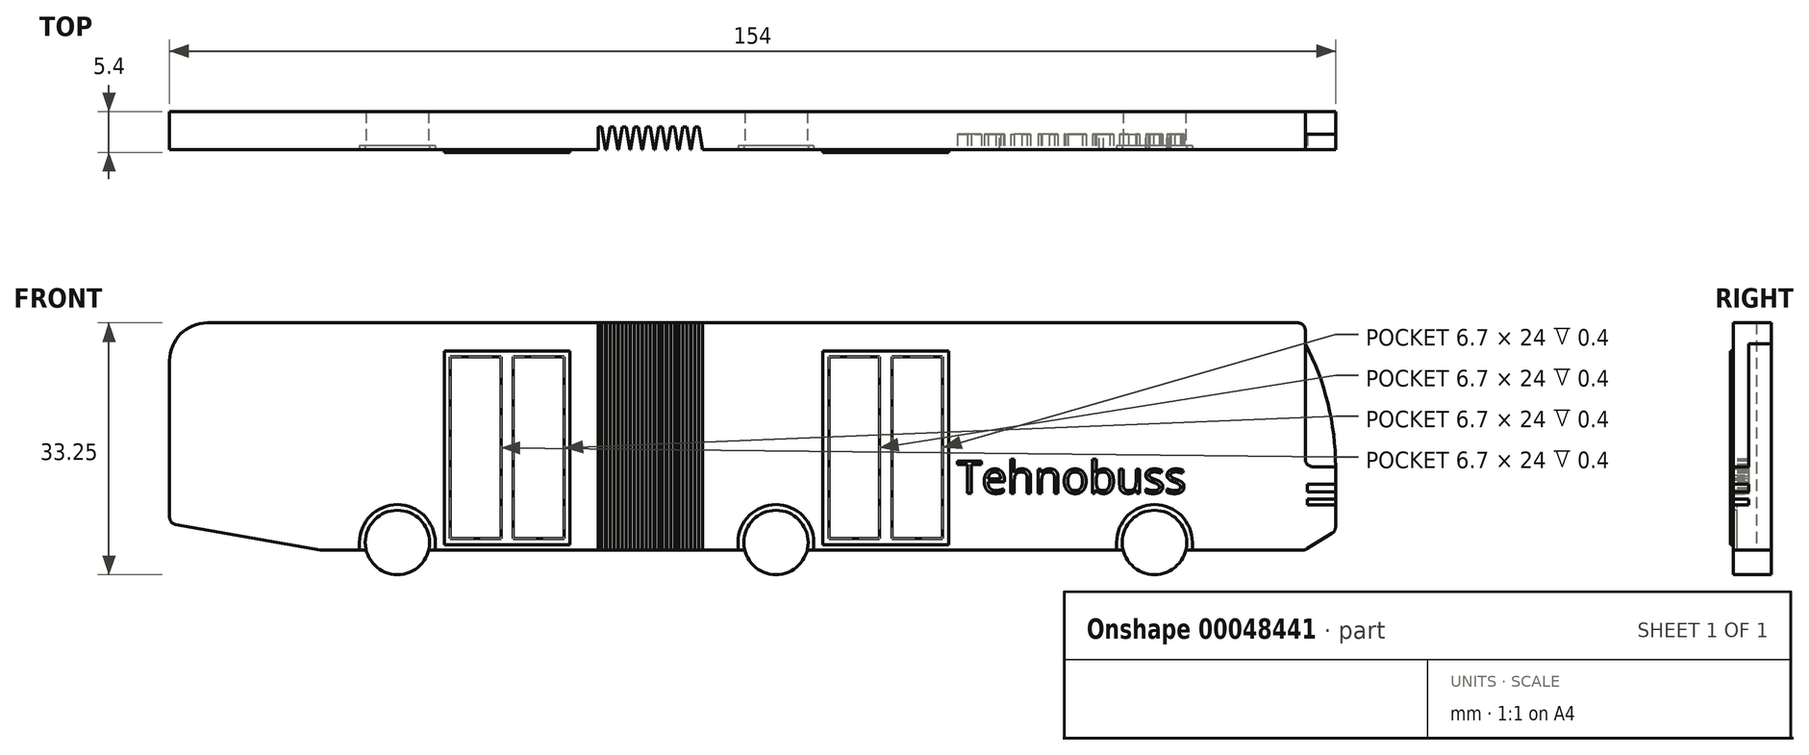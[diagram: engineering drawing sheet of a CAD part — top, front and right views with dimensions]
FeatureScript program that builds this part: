
annotation { "Feature Type Name" : "Feature", "Feature Type Description" : "" }
export const myFeature = defineFeature(function(context is Context, id is Id, definition is map)
    precondition{}
    {
        {
            var Q0;
            Q0=qCreatedBy(makeId("Front.planeOp"),FACE);
            var sketch = newSketch(context, id + "F0", { "sketchPlane" : qUnion([Q0])});
            skLineSegment(sketch, "E0.rect.bottom", {"start": v(75, 15) * mm, "end": v(-70, 15) * mm});
            skLineSegment(sketch, "E0.rect.top", {"start": v(75, -15) * mm, "end": v(-75, -15) * mm});
            skLineSegment(sketch, "E0.rect.left", {"start": v(75, 15) * mm, "end": v(75, -15) * mm});
            skLineSegment(sketch, "E0.rect.right", {"start": v(-75, 10) * mm, "end": v(-75, -15) * mm});
            skPoint(sketch, "E0.rect.middle", {"position": v(0, 0) * mm});
            skPoint(sketch, "E1.visualSharp", {"position": v(-75, 15) * mm});
            skArc(sketch, "E1.filletArc", {"start": v(-70, 15) * mm, "mid": v(-73.54, 13.54) * mm, "end": v(-75, 10) * mm});
            skLineSegment(sketch, "E2", {"start": v(-75, -11.5) * mm, "end": v(-55, -15) * mm});
            skLineSegment(sketch, "E3", {"start": v(75, -15) * mm, "end": v(79, -12.5) * mm});
            skLineSegment(sketch, "E4", {"start": v(79, -12.5) * mm, "end": v(79, -4) * mm});
            skArc(sketch, "E5", {"start": v(79, -4) * mm, "mid": v(77.99, 4.37) * mm, "end": v(75, 12.25) * mm});
            skSolve(sketch);
        }
        {
            var Q0;
            {var subQ3=sQuery(id+"F0.wireOp",EDGE,"E0.rect.bottom");Q0=makeQuery(id+"F0.imprint","IMPRINT",FACE,{"disambiguationData":[TD([[makeQuery(id+"F0.imprint","IMPRINT",EDGE,{"derivedFrom":subQ3}),1.0]])]});}
            var Q1;
            {var subQ1=sQuery(id+"F0.wireOp",EDGE,"E3");Q1=makeQuery(id+"F0.imprint","IMPRINT",FACE,{"disambiguationData":[TD([[makeQuery(id+"F0.imprint","IMPRINT",EDGE,{"derivedFrom":subQ1}),1.0]])]});}
            extrude(context, id + "F1", {"entities" : qUnion([Q0, Q1]), "depth" : 5 * mm});
        }
        {
            var Q0;
            Q0=makeQuery(id+"F1.opExtrude","SWEPT_EDGE",EDGE,{"disambiguationData":[OSD([sQuery(id+"F0.wireOp",EDGE,"E0.rect.right"),sQuery(id+"F0.wireOp",EDGE,"E2")])]});
            var Q1;
            Q1=makeQuery(id+"F1.opExtrude","SWEPT_EDGE",EDGE,{"disambiguationData":[OSD([sQuery(id+"F0.wireOp",EDGE,"E0.rect.top"),sQuery(id+"F0.wireOp",EDGE,"E2")])]});
            var Q2;
            Q2=makeQuery(id+"F1.opExtrude","SWEPT_EDGE",EDGE,{"disambiguationData":[OSD([sQuery(id+"F0.wireOp",EDGE,"E0.rect.top"),sQuery(id+"F0.wireOp",EDGE,"E0.rect.left"),sQuery(id+"F0.wireOp",EDGE,"E3")])]});
            var Q3;
            Q3=makeQuery(id+"F1.opExtrude","SWEPT_EDGE",EDGE,{"disambiguationData":[OSD([sQuery(id+"F0.wireOp",EDGE,"E3"),sQuery(id+"F0.wireOp",EDGE,"E4")])]});
            var Q4;
            Q4=makeQuery(id+"F1.opExtrude","SWEPT_EDGE",EDGE,{"disambiguationData":[OSD([sQuery(id+"F0.wireOp",EDGE,"E0.rect.bottom"),sQuery(id+"F0.wireOp",EDGE,"E0.rect.left")])]});
            fillet(context, id + "F2", {"entities" : qUnion([Q0, Q1, Q2, Q3, Q4]), "radius" : 1 * mm, "tangentPropagation" : true, "allowEdgeOverflow" : false});
        }
        {
            var Q0;
            Q0=makeQuery(id+"F1.opExtrude","CAP_FACE",FACE,{"disambiguationData":[OSD([sQuery(id+"F0.wireOp",EDGE,"E0.rect.bottom"),sQuery(id+"F0.wireOp",EDGE,"E0.rect.top"),sQuery(id+"F0.wireOp",EDGE,"E0.rect.left"),sQuery(id+"F0.wireOp",EDGE,"E0.rect.right"),sQuery(id+"F0.wireOp",EDGE,"E1.filletArc"),sQuery(id+"F0.wireOp",EDGE,"E2"),sQuery(id+"F0.wireOp",EDGE,"E3"),sQuery(id+"F0.wireOp",EDGE,"E4"),sQuery(id+"F0.wireOp",EDGE,"E5")])],"isStart":false});
            var sketch = newSketch(context, id + "F3", { "sketchPlane" : qUnion([Q0])});
            skCircle(sketch, "E6", {"center": v(-44.91, -14) * mm, "radius": 4.25 * mm});
            skCircle(sketch, "E7", {"center": v(5.09, -14) * mm, "radius": 4.25 * mm});
            skCircle(sketch, "E8", {"center": v(55.09, -14) * mm, "radius": 4.25 * mm});
            skLineSegment(sketch, "E9", {"start": v(-49.91, -15) * mm, "end": v(-49.91, -14) * mm});
            skLineSegment(sketch, "E10", {"start": v(-39.91, -15) * mm, "end": v(-39.91, -14) * mm});
            skArc(sketch, "E11", {"start": v(-39.91, -14) * mm, "mid": v(-44.91, -9) * mm, "end": v(-49.91, -14) * mm});
            skArc(sketch, "E12.1.0.0", {"start": v(10.09, -14) * mm, "mid": v(5.09, -9) * mm, "end": v(0.09, -14) * mm});
            skLineSegment(sketch, "E12.1.0.1", {"start": v(10.09, -15) * mm, "end": v(10.09, -14) * mm});
            skLineSegment(sketch, "E12.1.0.2", {"start": v(0.09, -15) * mm, "end": v(0.09, -14) * mm});
            skArc(sketch, "E12.2.0.0", {"start": v(60.09, -14) * mm, "mid": v(55.09, -9) * mm, "end": v(50.09, -14) * mm});
            skLineSegment(sketch, "E12.2.0.1", {"start": v(60.09, -15) * mm, "end": v(60.09, -14) * mm});
            skLineSegment(sketch, "E12.2.0.2", {"start": v(50.09, -15) * mm, "end": v(50.09, -14) * mm});
            skLineSegment(sketch, "E12.direction1", {"start": v(-49.91, -14) * mm, "end": v(0.09, -14) * mm, "construction": true});
            skSolve(sketch);
        }
        {
            var Q0;
            {var subQ5=sQuery(id+"F3.wireOp",EDGE,"E9");Q0=makeQuery(id+"F3.imprint","IMPRINT",FACE,{"disambiguationData":[TD([[makeQuery(id+"F3.imprint","IMPRINT",EDGE,{"derivedFrom":subQ5}),-1.0]])]});}
            var Q1;
            {var subQ0=makeQuery(id+"F1.opExtrude","CAP_EDGE",EDGE,{"disambiguationData":[OSD([sQuery(id+"F0.wireOp",EDGE,"E0.rect.top")])],"isStart":false});var subQ1=sQuery(id+"F3.wireOp",EDGE,"E6");var subQ3=makeQuery(id+"F3.imprint","INTERSECT",VERTEX,{"disambiguationData":[OD(0.0)],"derivedFrom":[subQ0,subQ1]});Q1=makeQuery(id+"F3.imprint","IMPRINT",FACE,{"disambiguationData":[TD([[makeQuery(id+"F3.imprint","IMPRINT",EDGE,{"disambiguationData":[TD([[subQ3,1.0]])],"derivedFrom":subQ1}),1.0]])]});}
            var Q2;
            Q2=makeQuery(id+"F3.imprint","IMPRINT",FACE,{"disambiguationData":[TD([[makeQuery(id+"F3.imprint","IMPRINT",EDGE,{"derivedFrom":sQuery(id+"F3.wireOp",EDGE,"E12.2.0.0")}),1.0]])]});
            var Q3;
            {var subQ0=makeQuery(id+"F1.opExtrude","CAP_EDGE",EDGE,{"disambiguationData":[OSD([sQuery(id+"F0.wireOp",EDGE,"E0.rect.top")])],"isStart":false});var subQ1=sQuery(id+"F3.wireOp",EDGE,"E8");var subQ3=makeQuery(id+"F3.imprint","INTERSECT",VERTEX,{"disambiguationData":[OD(0.0)],"derivedFrom":[subQ0,subQ1]});Q3=makeQuery(id+"F3.imprint","IMPRINT",FACE,{"disambiguationData":[TD([[makeQuery(id+"F3.imprint","IMPRINT",EDGE,{"disambiguationData":[TD([[subQ3,-1.0]])],"derivedFrom":subQ1}),1.0]])]});}
            var Q4;
            Q4=makeQuery(id+"F3.imprint","IMPRINT",FACE,{"disambiguationData":[TD([[makeQuery(id+"F3.imprint","IMPRINT",EDGE,{"derivedFrom":sQuery(id+"F3.wireOp",EDGE,"E12.1.0.0")}),1.0]])]});
            var Q5;
            {var subQ0=makeQuery(id+"F1.opExtrude","CAP_EDGE",EDGE,{"disambiguationData":[OSD([sQuery(id+"F0.wireOp",EDGE,"E0.rect.top")])],"isStart":false});var subQ1=sQuery(id+"F3.wireOp",EDGE,"E7");var subQ3=makeQuery(id+"F3.imprint","INTERSECT",VERTEX,{"disambiguationData":[OD(0.0)],"derivedFrom":[subQ0,subQ1]});Q5=makeQuery(id+"F3.imprint","IMPRINT",FACE,{"disambiguationData":[TD([[makeQuery(id+"F3.imprint","IMPRINT",EDGE,{"disambiguationData":[TD([[subQ3,-1.0]])],"derivedFrom":subQ1}),1.0]])]});}
            extrude(context, id + "F4", {"entities" : qUnion([Q0, Q1, Q2, Q3, Q4, Q5]), "operationType" : NewBodyOperationType.REMOVE, "oppositeDirection" : true, "depth" : .5 * mm});
        }
        {
            var Q0;
            {var subQ0=makeQuery(id+"F1.opExtrude","CAP_EDGE",EDGE,{"disambiguationData":[OSD([sQuery(id+"F0.wireOp",EDGE,"E0.rect.top")])],"isStart":false});var subQ1=sQuery(id+"F3.wireOp",EDGE,"E6");var subQ3=makeQuery(id+"F3.imprint","INTERSECT",VERTEX,{"disambiguationData":[OD(0.0)],"derivedFrom":[subQ0,subQ1]});Q0=makeQuery(id+"F3.imprint","IMPRINT",FACE,{"disambiguationData":[TD([[makeQuery(id+"F3.imprint","IMPRINT",EDGE,{"disambiguationData":[TD([[subQ3,-1.0]])],"derivedFrom":subQ1}),1.0]])]});}
            var Q1;
            {var subQ0=makeQuery(id+"F1.opExtrude","CAP_EDGE",EDGE,{"disambiguationData":[OSD([sQuery(id+"F0.wireOp",EDGE,"E0.rect.top")])],"isStart":false});var subQ1=sQuery(id+"F3.wireOp",EDGE,"E6");var subQ3=makeQuery(id+"F3.imprint","INTERSECT",VERTEX,{"disambiguationData":[OD(0.0)],"derivedFrom":[subQ0,subQ1]});Q1=makeQuery(id+"F3.imprint","IMPRINT",FACE,{"disambiguationData":[TD([[makeQuery(id+"F3.imprint","IMPRINT",EDGE,{"disambiguationData":[TD([[subQ3,1.0]])],"derivedFrom":subQ1}),1.0]])]});}
            var Q2;
            {var subQ0=makeQuery(id+"F1.opExtrude","CAP_EDGE",EDGE,{"disambiguationData":[OSD([sQuery(id+"F0.wireOp",EDGE,"E0.rect.top")])],"isStart":false});var subQ1=sQuery(id+"F3.wireOp",EDGE,"E7");var subQ3=makeQuery(id+"F3.imprint","INTERSECT",VERTEX,{"disambiguationData":[OD(0.0)],"derivedFrom":[subQ0,subQ1]});Q2=makeQuery(id+"F3.imprint","IMPRINT",FACE,{"disambiguationData":[TD([[makeQuery(id+"F3.imprint","IMPRINT",EDGE,{"disambiguationData":[TD([[subQ3,1.0]])],"derivedFrom":subQ1}),1.0]])]});}
            var Q3;
            {var subQ0=makeQuery(id+"F1.opExtrude","CAP_EDGE",EDGE,{"disambiguationData":[OSD([sQuery(id+"F0.wireOp",EDGE,"E0.rect.top")])],"isStart":false});var subQ1=sQuery(id+"F3.wireOp",EDGE,"E7");var subQ3=makeQuery(id+"F3.imprint","INTERSECT",VERTEX,{"disambiguationData":[OD(0.0)],"derivedFrom":[subQ0,subQ1]});Q3=makeQuery(id+"F3.imprint","IMPRINT",FACE,{"disambiguationData":[TD([[makeQuery(id+"F3.imprint","IMPRINT",EDGE,{"disambiguationData":[TD([[subQ3,-1.0]])],"derivedFrom":subQ1}),1.0]])]});}
            var Q4;
            {var subQ0=makeQuery(id+"F1.opExtrude","CAP_EDGE",EDGE,{"disambiguationData":[OSD([sQuery(id+"F0.wireOp",EDGE,"E0.rect.top")])],"isStart":false});var subQ1=sQuery(id+"F3.wireOp",EDGE,"E8");var subQ3=makeQuery(id+"F3.imprint","INTERSECT",VERTEX,{"disambiguationData":[OD(0.0)],"derivedFrom":[subQ0,subQ1]});Q4=makeQuery(id+"F3.imprint","IMPRINT",FACE,{"disambiguationData":[TD([[makeQuery(id+"F3.imprint","IMPRINT",EDGE,{"disambiguationData":[TD([[subQ3,1.0]])],"derivedFrom":subQ1}),1.0]])]});}
            var Q5;
            {var subQ0=makeQuery(id+"F1.opExtrude","CAP_EDGE",EDGE,{"disambiguationData":[OSD([sQuery(id+"F0.wireOp",EDGE,"E0.rect.top")])],"isStart":false});var subQ1=sQuery(id+"F3.wireOp",EDGE,"E8");var subQ3=makeQuery(id+"F3.imprint","INTERSECT",VERTEX,{"disambiguationData":[OD(0.0)],"derivedFrom":[subQ0,subQ1]});Q5=makeQuery(id+"F3.imprint","IMPRINT",FACE,{"disambiguationData":[TD([[makeQuery(id+"F3.imprint","IMPRINT",EDGE,{"disambiguationData":[TD([[subQ3,-1.0]])],"derivedFrom":subQ1}),1.0]])]});}
            extrude(context, id + "F5", {"entities" : qUnion([Q0, Q1, Q2, Q3, Q4, Q5]), "operationType" : NewBodyOperationType.ADD, "oppositeDirection" : true, "depth" : 5 * mm});
        }
        {
            var Q0;
            Q0=makeQuery(id+"F1.opExtrude","CAP_FACE",FACE,{"disambiguationData":[OSD([sQuery(id+"F0.wireOp",EDGE,"E0.rect.bottom"),sQuery(id+"F0.wireOp",EDGE,"E0.rect.top"),sQuery(id+"F0.wireOp",EDGE,"E0.rect.left"),sQuery(id+"F0.wireOp",EDGE,"E0.rect.right"),sQuery(id+"F0.wireOp",EDGE,"E1.filletArc"),sQuery(id+"F0.wireOp",EDGE,"E2"),sQuery(id+"F0.wireOp",EDGE,"E3"),sQuery(id+"F0.wireOp",EDGE,"E4"),sQuery(id+"F0.wireOp",EDGE,"E5")])],"isStart":false});
            var sketch = newSketch(context, id + "F6", { "sketchPlane" : qUnion([Q0])});
            skLineSegment(sketch, "E13.bottom", {"start": v(-19.41, 15) * mm, "end": v(-4.41, 15) * mm});
            skLineSegment(sketch, "E13.top", {"start": v(-19.41, -15) * mm, "end": v(-4.41, -15) * mm});
            skLineSegment(sketch, "E13.left", {"start": v(-19.41, 15) * mm, "end": v(-19.41, -15) * mm});
            skLineSegment(sketch, "E13.right", {"start": v(-4.41, 15) * mm, "end": v(-4.41, -15) * mm});
            skLineSegment(sketch, "E14", {"start": v(-18.41, 15) * mm, "end": v(-18.41, -15) * mm});
            skLineSegment(sketch, "E15", {"start": v(-17.91, 15) * mm, "end": v(-17.91, -15) * mm});
            skLineSegment(sketch, "E16.1.0.0", {"start": v(-16.31, 15) * mm, "end": v(-16.31, -15) * mm});
            skLineSegment(sketch, "E16.1.0.1", {"start": v(-16.81, 15) * mm, "end": v(-16.81, -15) * mm});
            skLineSegment(sketch, "E16.2.0.0", {"start": v(-14.71, 15) * mm, "end": v(-14.71, -15) * mm});
            skLineSegment(sketch, "E16.2.0.1", {"start": v(-15.21, 15) * mm, "end": v(-15.21, -15) * mm});
            skLineSegment(sketch, "E16.3.0.0", {"start": v(-13.11, 15) * mm, "end": v(-13.11, -15) * mm});
            skLineSegment(sketch, "E16.3.0.1", {"start": v(-13.61, 15) * mm, "end": v(-13.61, -15) * mm});
            skLineSegment(sketch, "E16.4.0.0", {"start": v(-11.51, 15) * mm, "end": v(-11.51, -15) * mm});
            skLineSegment(sketch, "E16.4.0.1", {"start": v(-12.01, 15) * mm, "end": v(-12.01, -15) * mm});
            skLineSegment(sketch, "E16.5.0.0", {"start": v(-9.91, 15) * mm, "end": v(-9.91, -15) * mm});
            skLineSegment(sketch, "E16.5.0.1", {"start": v(-10.41, 15) * mm, "end": v(-10.41, -15) * mm});
            skLineSegment(sketch, "E16.6.0.0", {"start": v(-8.31, 15) * mm, "end": v(-8.31, -15) * mm});
            skLineSegment(sketch, "E16.6.0.1", {"start": v(-8.81, 15) * mm, "end": v(-8.81, -15) * mm});
            skLineSegment(sketch, "E16.7.0.0", {"start": v(-6.71, 15) * mm, "end": v(-6.71, -15) * mm});
            skLineSegment(sketch, "E16.7.0.1", {"start": v(-7.21, 15) * mm, "end": v(-7.21, -15) * mm});
            skLineSegment(sketch, "E16.8.0.0", {"start": v(-5.11, 15) * mm, "end": v(-5.11, -15) * mm});
            skLineSegment(sketch, "E16.8.0.1", {"start": v(-5.61, 15) * mm, "end": v(-5.61, -15) * mm});
            skLineSegment(sketch, "E16.direction1", {"start": v(-17.91, -15) * mm, "end": v(-16.31, -15) * mm, "construction": true});
            skSolve(sketch);
        }
        {
            var Q0;
            {var subQ2=sQuery(id+"F6.wireOp",EDGE,"E14");Q0=makeQuery(id+"F6.imprint","IMPRINT",FACE,{"disambiguationData":[TD([[makeQuery(id+"F6.imprint","IMPRINT",EDGE,{"derivedFrom":subQ2}),1.0]])]});}
            var Q1;
            {var subQ2=sQuery(id+"F6.wireOp",EDGE,"E16.1.0.0");Q1=makeQuery(id+"F6.imprint","IMPRINT",FACE,{"disambiguationData":[TD([[makeQuery(id+"F6.imprint","IMPRINT",EDGE,{"derivedFrom":subQ2}),-1.0]])]});}
            var Q2;
            {var subQ2=sQuery(id+"F6.wireOp",EDGE,"E16.2.0.0");Q2=makeQuery(id+"F6.imprint","IMPRINT",FACE,{"disambiguationData":[TD([[makeQuery(id+"F6.imprint","IMPRINT",EDGE,{"derivedFrom":subQ2}),-1.0]])]});}
            var Q3;
            {var subQ2=sQuery(id+"F6.wireOp",EDGE,"E16.3.0.0");Q3=makeQuery(id+"F6.imprint","IMPRINT",FACE,{"disambiguationData":[TD([[makeQuery(id+"F6.imprint","IMPRINT",EDGE,{"derivedFrom":subQ2}),-1.0]])]});}
            var Q4;
            {var subQ2=sQuery(id+"F6.wireOp",EDGE,"E16.4.0.0");Q4=makeQuery(id+"F6.imprint","IMPRINT",FACE,{"disambiguationData":[TD([[makeQuery(id+"F6.imprint","IMPRINT",EDGE,{"derivedFrom":subQ2}),-1.0]])]});}
            var Q5;
            {var subQ2=sQuery(id+"F6.wireOp",EDGE,"E16.5.0.0");Q5=makeQuery(id+"F6.imprint","IMPRINT",FACE,{"disambiguationData":[TD([[makeQuery(id+"F6.imprint","IMPRINT",EDGE,{"derivedFrom":subQ2}),-1.0]])]});}
            var Q6;
            {var subQ2=sQuery(id+"F6.wireOp",EDGE,"E16.6.0.0");Q6=makeQuery(id+"F6.imprint","IMPRINT",FACE,{"disambiguationData":[TD([[makeQuery(id+"F6.imprint","IMPRINT",EDGE,{"derivedFrom":subQ2}),-1.0]])]});}
            var Q7;
            {var subQ2=sQuery(id+"F6.wireOp",EDGE,"E16.7.0.0");Q7=makeQuery(id+"F6.imprint","IMPRINT",FACE,{"disambiguationData":[TD([[makeQuery(id+"F6.imprint","IMPRINT",EDGE,{"derivedFrom":subQ2}),-1.0]])]});}
            var Q8;
            {var subQ2=sQuery(id+"F6.wireOp",EDGE,"E16.8.0.0");Q8=makeQuery(id+"F6.imprint","IMPRINT",FACE,{"disambiguationData":[TD([[makeQuery(id+"F6.imprint","IMPRINT",EDGE,{"derivedFrom":subQ2}),-1.0]])]});}
            extrude(context, id + "F7", {"entities" : qUnion([Q0, Q1, Q2, Q3, Q4, Q5, Q6, Q7, Q8]), "operationType" : NewBodyOperationType.REMOVE, "oppositeDirection" : true, "depth" : 3 * mm});
        }
        {
            var Q0;
            Q0=makeQuery(id+"F7.boolean.opBoolean","COPY",EDGE,{"derivedFrom":makeQuery(id+"F7.opExtrude","CAP_EDGE",EDGE,{"disambiguationData":[OSD([sQuery(id+"F6.wireOp",EDGE,"E14")])],"isStart":true})});
            var Q1;
            Q1=makeQuery(id+"F7.boolean.opBoolean","COPY",EDGE,{"derivedFrom":makeQuery(id+"F7.opExtrude","CAP_EDGE",EDGE,{"disambiguationData":[OSD([sQuery(id+"F6.wireOp",EDGE,"E16.1.0.1")])],"isStart":true})});
            var Q2;
            Q2=makeQuery(id+"F7.boolean.opBoolean","COPY",EDGE,{"derivedFrom":makeQuery(id+"F7.opExtrude","CAP_EDGE",EDGE,{"disambiguationData":[OSD([sQuery(id+"F6.wireOp",EDGE,"E16.2.0.1")])],"isStart":true})});
            var Q3;
            Q3=makeQuery(id+"F7.boolean.opBoolean","COPY",EDGE,{"derivedFrom":makeQuery(id+"F7.opExtrude","CAP_EDGE",EDGE,{"disambiguationData":[OSD([sQuery(id+"F6.wireOp",EDGE,"E16.3.0.1")])],"isStart":true})});
            var Q4;
            Q4=makeQuery(id+"F7.boolean.opBoolean","COPY",EDGE,{"derivedFrom":makeQuery(id+"F7.opExtrude","CAP_EDGE",EDGE,{"disambiguationData":[OSD([sQuery(id+"F6.wireOp",EDGE,"E16.4.0.1")])],"isStart":true})});
            var Q5;
            Q5=makeQuery(id+"F7.boolean.opBoolean","COPY",EDGE,{"derivedFrom":makeQuery(id+"F7.opExtrude","CAP_EDGE",EDGE,{"disambiguationData":[OSD([sQuery(id+"F6.wireOp",EDGE,"E16.5.0.1")])],"isStart":true})});
            var Q6;
            Q6=makeQuery(id+"F7.boolean.opBoolean","COPY",EDGE,{"derivedFrom":makeQuery(id+"F7.opExtrude","CAP_EDGE",EDGE,{"disambiguationData":[OSD([sQuery(id+"F6.wireOp",EDGE,"E16.6.0.1")])],"isStart":true})});
            var Q7;
            Q7=makeQuery(id+"F7.boolean.opBoolean","COPY",EDGE,{"derivedFrom":makeQuery(id+"F7.opExtrude","CAP_EDGE",EDGE,{"disambiguationData":[OSD([sQuery(id+"F6.wireOp",EDGE,"E16.7.0.1")])],"isStart":true})});
            var Q8;
            Q8=makeQuery(id+"F7.boolean.opBoolean","COPY",EDGE,{"derivedFrom":makeQuery(id+"F7.opExtrude","CAP_EDGE",EDGE,{"disambiguationData":[OSD([sQuery(id+"F6.wireOp",EDGE,"E16.8.0.1")])],"isStart":true})});
            chamfer(context, id + "F8", {"entities" : qUnion([Q0, Q1, Q2, Q3, Q4, Q5, Q6, Q7, Q8]), "chamferType" : ChamferType.TWO_OFFSETS, "width1" : 3 * mm, "oppositeDirection" : false, "width2" : .5 * mm, "tangentPropagation" : true});
        }
        {
            var Q0;
            Q0=makeQuery(id+"F7.boolean.opBoolean","COPY",EDGE,{"derivedFrom":makeQuery(id+"F7.opExtrude","CAP_EDGE",EDGE,{"disambiguationData":[OSD([sQuery(id+"F6.wireOp",EDGE,"E15")])],"isStart":true})});
            var Q1;
            Q1=makeQuery(id+"F7.boolean.opBoolean","COPY",EDGE,{"derivedFrom":makeQuery(id+"F7.opExtrude","CAP_EDGE",EDGE,{"disambiguationData":[OSD([sQuery(id+"F6.wireOp",EDGE,"E16.1.0.0")])],"isStart":true})});
            var Q2;
            Q2=makeQuery(id+"F7.boolean.opBoolean","COPY",EDGE,{"derivedFrom":makeQuery(id+"F7.opExtrude","CAP_EDGE",EDGE,{"disambiguationData":[OSD([sQuery(id+"F6.wireOp",EDGE,"E16.2.0.0")])],"isStart":true})});
            var Q3;
            Q3=makeQuery(id+"F7.boolean.opBoolean","COPY",EDGE,{"derivedFrom":makeQuery(id+"F7.opExtrude","CAP_EDGE",EDGE,{"disambiguationData":[OSD([sQuery(id+"F6.wireOp",EDGE,"E16.3.0.0")])],"isStart":true})});
            var Q4;
            Q4=makeQuery(id+"F7.boolean.opBoolean","COPY",EDGE,{"derivedFrom":makeQuery(id+"F7.opExtrude","CAP_EDGE",EDGE,{"disambiguationData":[OSD([sQuery(id+"F6.wireOp",EDGE,"E16.4.0.0")])],"isStart":true})});
            var Q5;
            Q5=makeQuery(id+"F7.boolean.opBoolean","COPY",EDGE,{"derivedFrom":makeQuery(id+"F7.opExtrude","CAP_EDGE",EDGE,{"disambiguationData":[OSD([sQuery(id+"F6.wireOp",EDGE,"E16.5.0.0")])],"isStart":true})});
            var Q6;
            Q6=makeQuery(id+"F7.boolean.opBoolean","COPY",EDGE,{"derivedFrom":makeQuery(id+"F7.opExtrude","CAP_EDGE",EDGE,{"disambiguationData":[OSD([sQuery(id+"F6.wireOp",EDGE,"E16.6.0.0")])],"isStart":true})});
            var Q7;
            Q7=makeQuery(id+"F7.boolean.opBoolean","COPY",EDGE,{"derivedFrom":makeQuery(id+"F7.opExtrude","CAP_EDGE",EDGE,{"disambiguationData":[OSD([sQuery(id+"F6.wireOp",EDGE,"E16.7.0.0")])],"isStart":true})});
            var Q8;
            Q8=makeQuery(id+"F7.boolean.opBoolean","COPY",EDGE,{"derivedFrom":makeQuery(id+"F7.opExtrude","CAP_EDGE",EDGE,{"disambiguationData":[OSD([sQuery(id+"F6.wireOp",EDGE,"E16.8.0.0")])],"isStart":true})});
            chamfer(context, id + "F9", {"entities" : qUnion([Q0, Q1, Q2, Q3, Q4, Q5, Q6, Q7, Q8]), "chamferType" : ChamferType.TWO_OFFSETS, "width1" : .5 * mm, "oppositeDirection" : false, "width2" : 3 * mm, "tangentPropagation" : true});
        }
        {
            var Q0;
            {var subQ0=sQuery(id+"F0.wireOp",EDGE,"E0.rect.bottom");var subQ1=sQuery(id+"F0.wireOp",EDGE,"E0.rect.top");var subQ2=sQuery(id+"F0.wireOp",EDGE,"E0.rect.left");var subQ3=sQuery(id+"F0.wireOp",EDGE,"E3");var subQ4=sQuery(id+"F0.wireOp",EDGE,"E4");var subQ5=sQuery(id+"F0.wireOp",EDGE,"E5");Q0=makeQuery(id+"F7.boolean.opBoolean","SPLIT",FACE,{"disambiguationData":[TD([makeQuery(id+"F1.opExtrude","SWEPT_FACE",FACE,{"disambiguationData":[OSD([subQ2])]})])],"derivedFrom":makeQuery(id+"F1.opExtrude","CAP_FACE",FACE,{"disambiguationData":[OSD([subQ0,subQ1,subQ2,sQuery(id+"F0.wireOp",EDGE,"E0.rect.right"),sQuery(id+"F0.wireOp",EDGE,"E1.filletArc"),sQuery(id+"F0.wireOp",EDGE,"E2"),subQ3,subQ4,subQ5])],"isStart":false})});}
            var sketch = newSketch(context, id + "F10", { "sketchPlane" : qUnion([Q0])});
            skLineSegment(sketch, "E17.bottom", {"start": v(12.09, -13.5) * mm, "end": v(27.09, -13.5) * mm});
            skLineSegment(sketch, "E17.top", {"start": v(12.09, 10.5) * mm, "end": v(27.09, 10.5) * mm});
            skLineSegment(sketch, "E17.left", {"start": v(12.09, -13.5) * mm, "end": v(12.09, 10.5) * mm});
            skLineSegment(sketch, "E17.right", {"start": v(27.09, -13.5) * mm, "end": v(27.09, 10.5) * mm});
            skLineSegment(sketch, "E18", {"start": v(18.79, 10.5) * mm, "end": v(18.79, -13.5) * mm});
            skLineSegment(sketch, "E19", {"start": v(20.39, 10.5) * mm, "end": v(20.39, -13.5) * mm});
            skLineSegment(sketch, "E20.0", {"start": v(11.29, 11.3) * mm, "end": v(27.89, 11.3) * mm});
            skLineSegment(sketch, "E20.1", {"start": v(11.29, -14.3) * mm, "end": v(11.29, 11.3) * mm});
            skLineSegment(sketch, "E20.2", {"start": v(11.29, -14.3) * mm, "end": v(27.89, -14.3) * mm});
            skLineSegment(sketch, "E20.3", {"start": v(27.89, -14.3) * mm, "end": v(27.89, 11.3) * mm});
            skLineSegment(sketch, "E21.1.0.0", {"start": v(-38.71, 11.3) * mm, "end": v(-22.11, 11.3) * mm});
            skLineSegment(sketch, "E21.1.0.1", {"start": v(-37.91, 10.5) * mm, "end": v(-22.91, 10.5) * mm});
            skLineSegment(sketch, "E21.1.0.2", {"start": v(-38.71, -14.3) * mm, "end": v(-38.71, 11.3) * mm});
            skLineSegment(sketch, "E21.1.0.3", {"start": v(-31.21, 10.5) * mm, "end": v(-31.21, -13.5) * mm});
            skLineSegment(sketch, "E21.1.0.4", {"start": v(-22.91, -13.5) * mm, "end": v(-22.91, 10.5) * mm});
            skLineSegment(sketch, "E21.1.0.5", {"start": v(-38.71, -14.3) * mm, "end": v(-22.11, -14.3) * mm});
            skLineSegment(sketch, "E21.1.0.6", {"start": v(-22.11, -14.3) * mm, "end": v(-22.11, 11.3) * mm});
            skLineSegment(sketch, "E21.1.0.7", {"start": v(-37.91, -13.5) * mm, "end": v(-22.91, -13.5) * mm});
            skLineSegment(sketch, "E21.1.0.8", {"start": v(-29.61, 10.5) * mm, "end": v(-29.61, -13.5) * mm});
            skLineSegment(sketch, "E21.1.0.9", {"start": v(-37.91, -13.5) * mm, "end": v(-37.91, 10.5) * mm});
            skLineSegment(sketch, "E21.direction1", {"start": v(11.29, 11.3) * mm, "end": v(-38.71, 11.3) * mm, "construction": true});
            skSolve(sketch);
        }
        {
            var Q0;
            {var subQ1=sQuery(id+"F10.wireOp",EDGE,"E21.1.0.3");Q0=makeQuery(id+"F10.imprint","IMPRINT",FACE,{"disambiguationData":[TD([[makeQuery(id+"F10.imprint","IMPRINT",EDGE,{"derivedFrom":subQ1}),1.0]])]});}
            var Q1;
            Q1=makeQuery(id+"F10.imprint","IMPRINT",FACE,{"disambiguationData":[TD([[makeQuery(id+"F10.imprint","IMPRINT",EDGE,{"derivedFrom":sQuery(id+"F10.wireOp",EDGE,"E21.1.0.0")}),-1.0]])]});
            var Q2;
            {var subQ0=sQuery(id+"F10.wireOp",EDGE,"E18");Q2=makeQuery(id+"F10.imprint","IMPRINT",FACE,{"disambiguationData":[TD([[makeQuery(id+"F10.imprint","IMPRINT",EDGE,{"derivedFrom":subQ0}),1.0]])]});}
            var Q3;
            {var subQ3=sQuery(id+"F10.wireOp",EDGE,"E17.left");Q3=makeQuery(id+"F10.imprint","IMPRINT",FACE,{"disambiguationData":[TD([[makeQuery(id+"F10.imprint","IMPRINT",EDGE,{"derivedFrom":subQ3}),1.0]])]});}
            extrude(context, id + "F11", {"entities" : qUnion([Q0, Q1, Q2, Q3]), "operationType" : NewBodyOperationType.ADD, "depth" : .4 * mm});
        }
        {
            var Q0;
            {var subQ0=sQuery(id+"F0.wireOp",EDGE,"E0.rect.bottom");var subQ1=sQuery(id+"F0.wireOp",EDGE,"E0.rect.top");var subQ2=sQuery(id+"F0.wireOp",EDGE,"E0.rect.left");var subQ3=sQuery(id+"F0.wireOp",EDGE,"E3");var subQ4=sQuery(id+"F0.wireOp",EDGE,"E4");var subQ5=sQuery(id+"F0.wireOp",EDGE,"E5");Q0=makeQuery(id+"F7.boolean.opBoolean","SPLIT",FACE,{"disambiguationData":[TD([makeQuery(id+"F1.opExtrude","SWEPT_FACE",FACE,{"disambiguationData":[OSD([subQ2])]})])],"derivedFrom":makeQuery(id+"F1.opExtrude","CAP_FACE",FACE,{"disambiguationData":[OSD([subQ0,subQ1,subQ2,sQuery(id+"F0.wireOp",EDGE,"E0.rect.right"),sQuery(id+"F0.wireOp",EDGE,"E1.filletArc"),sQuery(id+"F0.wireOp",EDGE,"E2"),subQ3,subQ4,subQ5])],"isStart":false})});}
            var sketch = newSketch(context, id + "F12", { "sketchPlane" : qUnion([Q0])});
            skText(sketch, "E22", { "text": "Tehnobuss", "fontName": "OpenSans-Regular.ttf"});
            const initialGuessF12  = {"E22": [0.029, -0.0075, 1, 0, 0.00425]};
            skSetInitialGuess(sketch, initialGuessF12);
            skSolve(sketch);
        }
        {
            var Q0;
            Q0 = qSketchRegion(id + "F12", true);
            extrude(context, id + "F13", {"entities" : qUnion([Q0]), "operationType" : NewBodyOperationType.REMOVE, "oppositeDirection" : true, "depth" : 2 * mm});
        }
        {
            var Q0;
            {var subQ0=sQuery(id+"F0.wireOp",EDGE,"E0.rect.bottom");var subQ1=sQuery(id+"F0.wireOp",EDGE,"E0.rect.top");var subQ2=sQuery(id+"F0.wireOp",EDGE,"E0.rect.left");var subQ3=sQuery(id+"F0.wireOp",EDGE,"E3");var subQ4=sQuery(id+"F0.wireOp",EDGE,"E4");var subQ5=sQuery(id+"F0.wireOp",EDGE,"E5");var subQ10=makeQuery(id+"F1.opExtrude","SWEPT_FACE",FACE,{"disambiguationData":[OSD([subQ2])]});var subQ15=makeQuery(id+"F1.opExtrude","SWEPT_FACE",FACE,{"disambiguationData":[OSD([subQ0])]});Q0=makeQuery(id+"F13.boolean.opBoolean","SPLIT",FACE,{"disambiguationData":[TD([subQ15])],"derivedFrom":makeQuery(id+"F11.boolean.opBoolean","SPLIT",FACE,{"disambiguationData":[TD([subQ15])],"derivedFrom":makeQuery(id+"F7.boolean.opBoolean","SPLIT",FACE,{"disambiguationData":[TD([subQ10])],"derivedFrom":makeQuery(id+"F1.opExtrude","CAP_FACE",FACE,{"disambiguationData":[OSD([subQ0,subQ1,subQ2,sQuery(id+"F0.wireOp",EDGE,"E0.rect.right"),sQuery(id+"F0.wireOp",EDGE,"E1.filletArc"),sQuery(id+"F0.wireOp",EDGE,"E2"),subQ3,subQ4,subQ5])],"isStart":false})})})});}
            var sketch = newSketch(context, id + "F14", { "sketchPlane" : qUnion([Q0])});
            skLineSegment(sketch, "E23", {"start": v(75.3, 11.66) * mm, "end": v(75.3, -4) * mm});
            skLineSegment(sketch, "E24", {"start": v(75.3, -4) * mm, "end": v(75, -4) * mm});
            skLineSegment(sketch, "E25", {"start": v(75, -4) * mm, "end": v(75, 12.25) * mm});
            skLineSegment(sketch, "E26.bottom", {"start": v(75.3, -4) * mm, "end": v(79, -4) * mm});
            skLineSegment(sketch, "E26.top", {"start": v(75.3, -4.3) * mm, "end": v(79, -4.3) * mm});
            skLineSegment(sketch, "E26.left", {"start": v(75.3, -4) * mm, "end": v(75.3, -4.3) * mm});
            skLineSegment(sketch, "E26.right", {"start": v(79, -4) * mm, "end": v(79, -4.3) * mm});
            skArc(sketch, "E27", {"start": v(75, -4) * mm, "mid": v(75.09, -4.21) * mm, "end": v(75.3, -4.3) * mm});
            skLineSegment(sketch, "E28.bottom", {"start": v(79, -6.3) * mm, "end": v(75.3, -6.3) * mm});
            skLineSegment(sketch, "E28.top", {"start": v(79, -7.3) * mm, "end": v(75.3, -7.3) * mm});
            skLineSegment(sketch, "E28.left", {"start": v(79, -6.3) * mm, "end": v(79, -7.3) * mm});
            skLineSegment(sketch, "E28.right", {"start": v(75.3, -6.3) * mm, "end": v(75.3, -7.3) * mm});
            skLineSegment(sketch, "E29.bottom", {"start": v(79, -8.3) * mm, "end": v(75.3, -8.3) * mm});
            skLineSegment(sketch, "E29.top", {"start": v(79, -9.05) * mm, "end": v(75.3, -9.05) * mm});
            skLineSegment(sketch, "E29.left", {"start": v(79, -8.3) * mm, "end": v(79, -9.05) * mm});
            skLineSegment(sketch, "E29.right", {"start": v(75.3, -8.3) * mm, "end": v(75.3, -9.05) * mm});
            skSolve(sketch);
        }
        {
            var Q0;
            {var subQ1=sQuery(id+"F14.wireOp",EDGE,"E23");Q0=makeQuery(id+"F14.imprint","IMPRINT",FACE,{"disambiguationData":[TD([[makeQuery(id+"F14.imprint","IMPRINT",EDGE,{"derivedFrom":subQ1}),1.0]])]});}
            var Q1;
            Q1=makeQuery(id+"F14.imprint","IMPRINT",FACE,{"disambiguationData":[TD([[makeQuery(id+"F14.imprint","IMPRINT",EDGE,{"derivedFrom":sQuery(id+"F14.wireOp",EDGE,"E28.bottom")}),1.0]])]});
            var Q2;
            Q2=makeQuery(id+"F14.imprint","IMPRINT",FACE,{"disambiguationData":[TD([[makeQuery(id+"F14.imprint","IMPRINT",EDGE,{"derivedFrom":sQuery(id+"F14.wireOp",EDGE,"E29.bottom")}),1.0]])]});
            var Q3;
            {var subQ1=sQuery(id+"F14.wireOp",EDGE,"E23");Q3=makeQuery(id+"F14.imprint","IMPRINT",FACE,{"disambiguationData":[TD([[makeQuery(id+"F14.imprint","IMPRINT",EDGE,{"derivedFrom":subQ1}),-1.0]])]});}
            extrude(context, id + "F15", {"entities" : qUnion([Q0, Q1, Q2, Q3]), "operationType" : NewBodyOperationType.REMOVE, "oppositeDirection" : true, "depth" : 2 * mm});
        }
        {
            var Q0;
            Q0=makeQuery(id+"F15.boolean.opBoolean","COPY",EDGE,{"derivedFrom":makeQuery(id+"F15.opExtrude","SWEPT_EDGE",EDGE,{"disambiguationData":[OSD([sQuery(id+"F14.wireOp",EDGE,"E24"),sQuery(id+"F14.wireOp",EDGE,"E25"),sQuery(id+"F14.wireOp",EDGE,"E27")])]})});
            fillet(context, id + "F16", {"entities" : qUnion([Q0]), "radius" : 1 * mm, "tangentPropagation" : true, "allowEdgeOverflow" : false});
        }
    });
